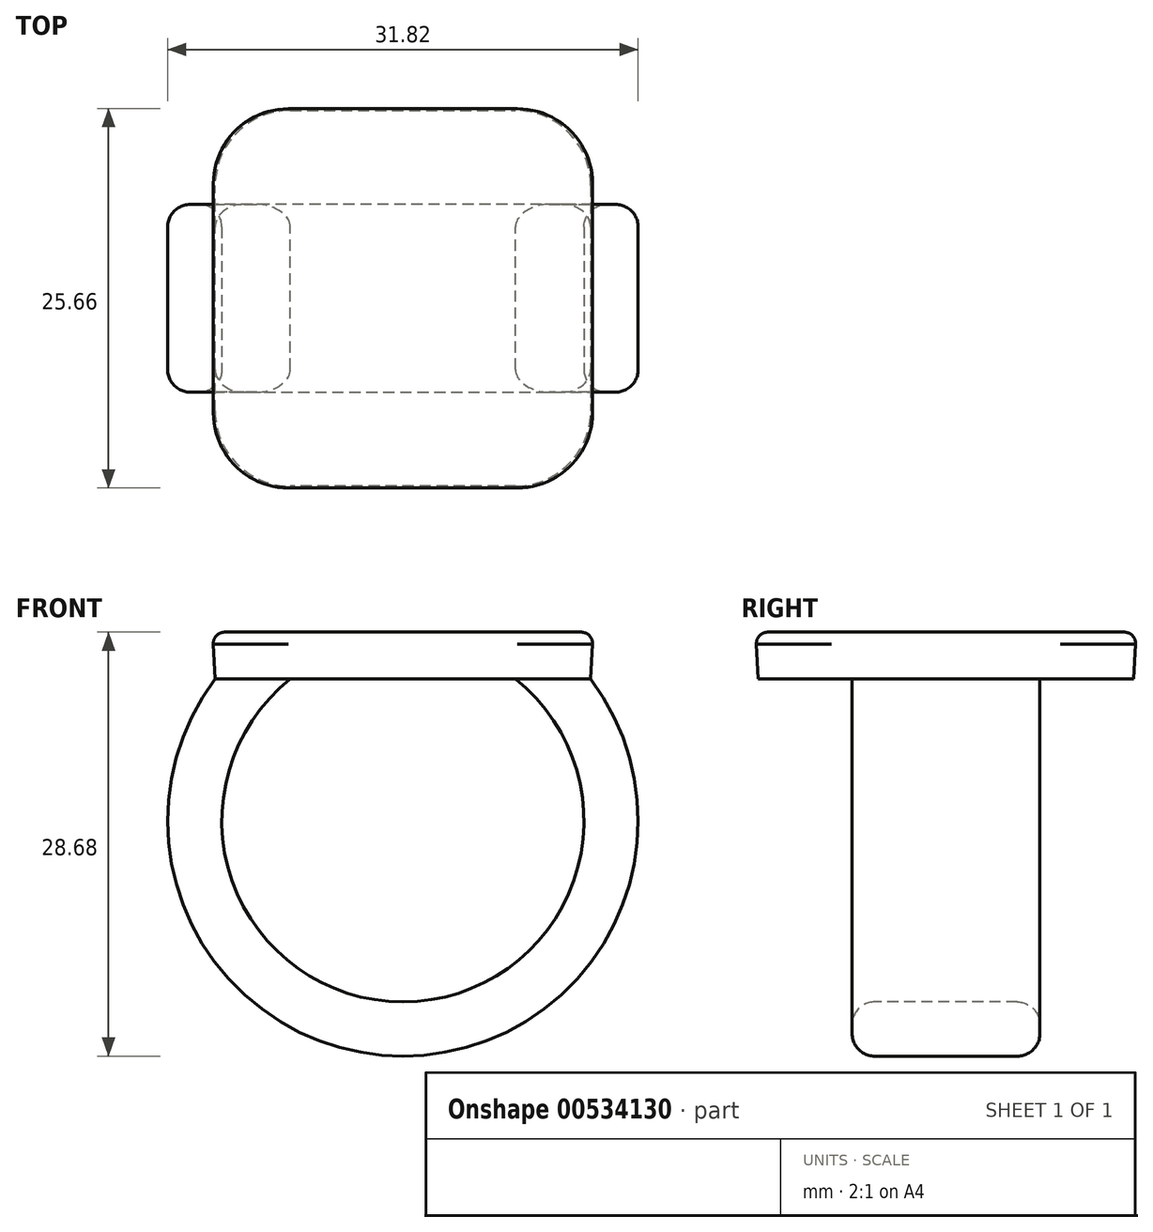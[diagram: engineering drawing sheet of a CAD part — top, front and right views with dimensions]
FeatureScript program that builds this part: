
annotation { "Feature Type Name" : "Feature", "Feature Type Description" : "" }
export const myFeature = defineFeature(function(context is Context, id is Id, definition is map)
    precondition{}
    {
        {
            var Q0;
            Q0=qCreatedBy(makeId("Top.planeOp"),FACE);
            var sketch = newSketch(context, id + "F0", { "sketchPlane" : qUnion([Q0])});
            skLineSegment(sketch, "E0.bottom", {"start": v(-12.7, -12.7) * mm, "end": v(12.7, -12.7) * mm});
            skLineSegment(sketch, "E0.top", {"start": v(-12.7, 12.7) * mm, "end": v(12.7, 12.7) * mm});
            skLineSegment(sketch, "E0.left", {"start": v(-12.7, -12.7) * mm, "end": v(-12.7, 12.7) * mm});
            skLineSegment(sketch, "E0.right", {"start": v(12.7, -12.7) * mm, "end": v(12.7, 12.7) * mm});
            skPoint(sketch, "E0.middle", {"position": v(0, 0) * mm});
            skSolve(sketch);
        }
        {
            var Q0;
            Q0 = qSketchRegion(id + "F0", true);
            extrude(context, id + "F1", {"entities" : qUnion([Q0]), "depth" : 3.17 * mm, "offsetDistance" : 25.4 * mm, "hasDraft" : true, "draftAngle" : 3 * degree});
        }
        {
            var Q0;
            Q0=qCreatedBy(makeId("Front.planeOp"),FACE);
            var sketch = newSketch(context, id + "F2", { "sketchPlane" : qUnion([Q0])});
            skArc(sketch, "E1", {"start": v(-10.16, 0) * mm, "mid": v(0, -23.56) * mm, "end": v(10.16, 0) * mm});
            skSolve(sketch);
        }
        {
            var Q0;
            Q0=makeQuery(id+"F1.opExtrude","CAP_FACE",FACE,{"disambiguationData":[OSD([sQuery(id+"F0.wireOp",EDGE,"E0.bottom"),sQuery(id+"F0.wireOp",EDGE,"E0.top"),sQuery(id+"F0.wireOp",EDGE,"E0.left"),sQuery(id+"F0.wireOp",EDGE,"E0.right")])],"isStart":true});
            var sketch = newSketch(context, id + "F3", { "sketchPlane" : qUnion([Q0])});
            skLineSegment(sketch, "E2.bottom", {"start": v(-12.7, 6.35) * mm, "end": v(-7.62, 6.35) * mm});
            skLineSegment(sketch, "E2.top", {"start": v(-12.7, -6.35) * mm, "end": v(-7.62, -6.35) * mm});
            skLineSegment(sketch, "E2.left", {"start": v(-12.7, 6.35) * mm, "end": v(-12.7, -6.35) * mm});
            skLineSegment(sketch, "E2.right", {"start": v(-7.62, 6.35) * mm, "end": v(-7.62, -6.35) * mm});
            skPoint(sketch, "E2.middle", {"position": v(-10.16, 0) * mm});
            skSolve(sketch);
        }
        {
            var Q0;
            Q0 = qSketchRegion(id + "F3", true);
            var Q1;
            Q1 = qConstructionFilter(qBodyType(qCreatedBy(id + "F2" ,EDGE), BodyType.WIRE), ConstructionObject.NO);
            sweep(context, id + "F4", {"operationType" : NewBodyOperationType.ADD, "profiles" : qUnion([Q0]), "path" : qUnion([Q1])});
        }
        {
            var Q0;
            Q0=qCreatedBy(makeId("Front.planeOp"),FACE);
            var sketch = newSketch(context, id + "F5", { "sketchPlane" : qUnion([Q0])});
            skLineSegment(sketch, "E3.1", {"start": v(10.01, -2.54) * mm, "end": v(10.16, 0) * mm});
            skArc(sketch, "E3.2", {"start": v(10.01, -2.54) * mm, "mid": v(8.9, -1.18) * mm, "end": v(7.62, 0) * mm});
            skPoint(sketch, "E4.orphan", {"position": v(12.7, 0) * mm});
            skLineSegment(sketch, "E5.trimOffspring", {"start": v(7.62, 0) * mm, "end": v(10.16, 0) * mm});
            skPoint(sketch, "E3.0.start.orphan", {"position": v(-12.7, 0) * mm});
            skPoint(sketch, "E6.orphan", {"position": v(-7.62, 0) * mm});
            skSolve(sketch);
        }
        {
            var Q0;
            Q0 = qSketchRegion(id + "F5", true);
            var Q1;
            Q1=makeQuery(id+"F4.opSweep","SWEPT_FACE",FACE,{"disambiguationData":[OSD([sQuery(id+"F2.wireOp",EDGE,"E1"),sQuery(id+"F3.wireOp",EDGE,"E2.bottom")])]});
            var Q2;
            Q2=makeQuery(id+"F4.opSweep","SWEPT_FACE",FACE,{"disambiguationData":[OSD([sQuery(id+"F2.wireOp",EDGE,"E1"),sQuery(id+"F3.wireOp",EDGE,"E2.top")])]});
            extrude(context, id + "F6", {"entities" : qUnion([Q0]), "operationType" : NewBodyOperationType.ADD, "endBound" : BoundingType.UP_TO_SURFACE, "depth" : 25.4 * mm, "endBoundEntityFace" : qUnion([Q1]), "offsetDistance" : 25.4 * mm, "hasSecondDirection" : true, "secondDirectionBound" : SecondDirectionBoundingType.UP_TO_SURFACE, "secondDirectionOppositeDirection" : true, "secondDirectionDepth" : 25.4 * mm, "secondDirectionBoundEntityFace" : qUnion([Q2])});
        }
        {
            var Q0;
            Q0=makeQuery(id+"F1.opExtrude","SWEPT_EDGE",EDGE,{"disambiguationData":[OSD([sQuery(id+"F0.wireOp",EDGE,"E0.top"),sQuery(id+"F0.wireOp",EDGE,"E0.right")])]});
            var Q1;
            Q1=makeQuery(id+"F1.opExtrude","SWEPT_EDGE",EDGE,{"disambiguationData":[OSD([sQuery(id+"F0.wireOp",EDGE,"E0.bottom"),sQuery(id+"F0.wireOp",EDGE,"E0.right")])]});
            var Q2;
            Q2=makeQuery(id+"F1.opExtrude","SWEPT_EDGE",EDGE,{"disambiguationData":[OSD([sQuery(id+"F0.wireOp",EDGE,"E0.bottom"),sQuery(id+"F0.wireOp",EDGE,"E0.left")])]});
            var Q3;
            Q3=makeQuery(id+"F1.opExtrude","SWEPT_EDGE",EDGE,{"disambiguationData":[OSD([sQuery(id+"F0.wireOp",EDGE,"E0.top"),sQuery(id+"F0.wireOp",EDGE,"E0.left")])]});
            fillet(context, id + "F7", {"entities" : qUnion([Q0, Q1, Q2, Q3]), "radius" : 5.08 * mm, "tangentPropagation" : true, "allowEdgeOverflow" : false});
        }
        {
            var Q0;
            {var subQ0=sQuery(id+"F3.wireOp",EDGE,"E2.top");var subQ1=sQuery(id+"F2.wireOp",EDGE,"E1");Q0=makeQuery(id+"F6.boolean.opBoolean","MERGE",EDGE,{"derivedFrom":[makeQuery(id+"F4.opSweep","SWEPT_EDGE",EDGE,{"disambiguationData":[OSD([subQ1,subQ0,sQuery(id+"F3.wireOp",EDGE,"E2.right")])]}),makeQuery(id+"F6.opExtrude","TWEAK_EDGE",EDGE,{"derivedFrom":[makeQuery(id+"F4.opSweep","SWEPT_FACE",FACE,{"disambiguationData":[OSD([subQ1,subQ0])]}),makeQuery(id+"F5.imprint","IMPRINT",EDGE,{"derivedFrom":sQuery(id+"F5.wireOp",EDGE,"E3.2")})]})]});}
            var Q1;
            {var subQ0=sQuery(id+"F3.wireOp",EDGE,"E2.bottom");var subQ1=sQuery(id+"F2.wireOp",EDGE,"E1");Q1=makeQuery(id+"F6.boolean.opBoolean","MERGE",EDGE,{"derivedFrom":[makeQuery(id+"F4.opSweep","SWEPT_EDGE",EDGE,{"disambiguationData":[OSD([subQ1,subQ0,sQuery(id+"F3.wireOp",EDGE,"E2.right")])]}),makeQuery(id+"F6.opExtrude","TWEAK_EDGE",EDGE,{"derivedFrom":[makeQuery(id+"F4.opSweep","SWEPT_FACE",FACE,{"disambiguationData":[OSD([subQ1,subQ0])]}),makeQuery(id+"F5.imprint","IMPRINT",EDGE,{"derivedFrom":sQuery(id+"F5.wireOp",EDGE,"E3.2")})]})]});}
            var Q2;
            Q2=makeQuery(id+"F4.opSweep","SWEPT_EDGE",EDGE,{"disambiguationData":[OSD([sQuery(id+"F0.wireOp",EDGE,"E0.left"),sQuery(id+"F2.wireOp",EDGE,"E1"),sQuery(id+"F3.wireOp",EDGE,"E2.bottom"),sQuery(id+"F3.wireOp",EDGE,"E2.left")])]});
            var Q3;
            Q3=makeQuery(id+"F4.opSweep","SWEPT_EDGE",EDGE,{"disambiguationData":[OSD([sQuery(id+"F0.wireOp",EDGE,"E0.left"),sQuery(id+"F2.wireOp",EDGE,"E1"),sQuery(id+"F3.wireOp",EDGE,"E2.top"),sQuery(id+"F3.wireOp",EDGE,"E2.left")])]});
            fillet(context, id + "F8", {"entities" : qUnion([Q0, Q1, Q2, Q3]), "radius" : 1.52 * mm, "tangentPropagation" : true, "allowEdgeOverflow" : false});
        }
        {
            var Q0;
            Q0=makeQuery(id+"F1.opExtrude","CAP_FACE",FACE,{"disambiguationData":[OSD([sQuery(id+"F0.wireOp",EDGE,"E0.bottom"),sQuery(id+"F0.wireOp",EDGE,"E0.top"),sQuery(id+"F0.wireOp",EDGE,"E0.left"),sQuery(id+"F0.wireOp",EDGE,"E0.right")])],"isStart":false});
            fillet(context, id + "F9", {"entities" : qUnion([Q0]), "radius" : 0.76 * mm, "tangentPropagation" : true, "allowEdgeOverflow" : false});
        }
    });
